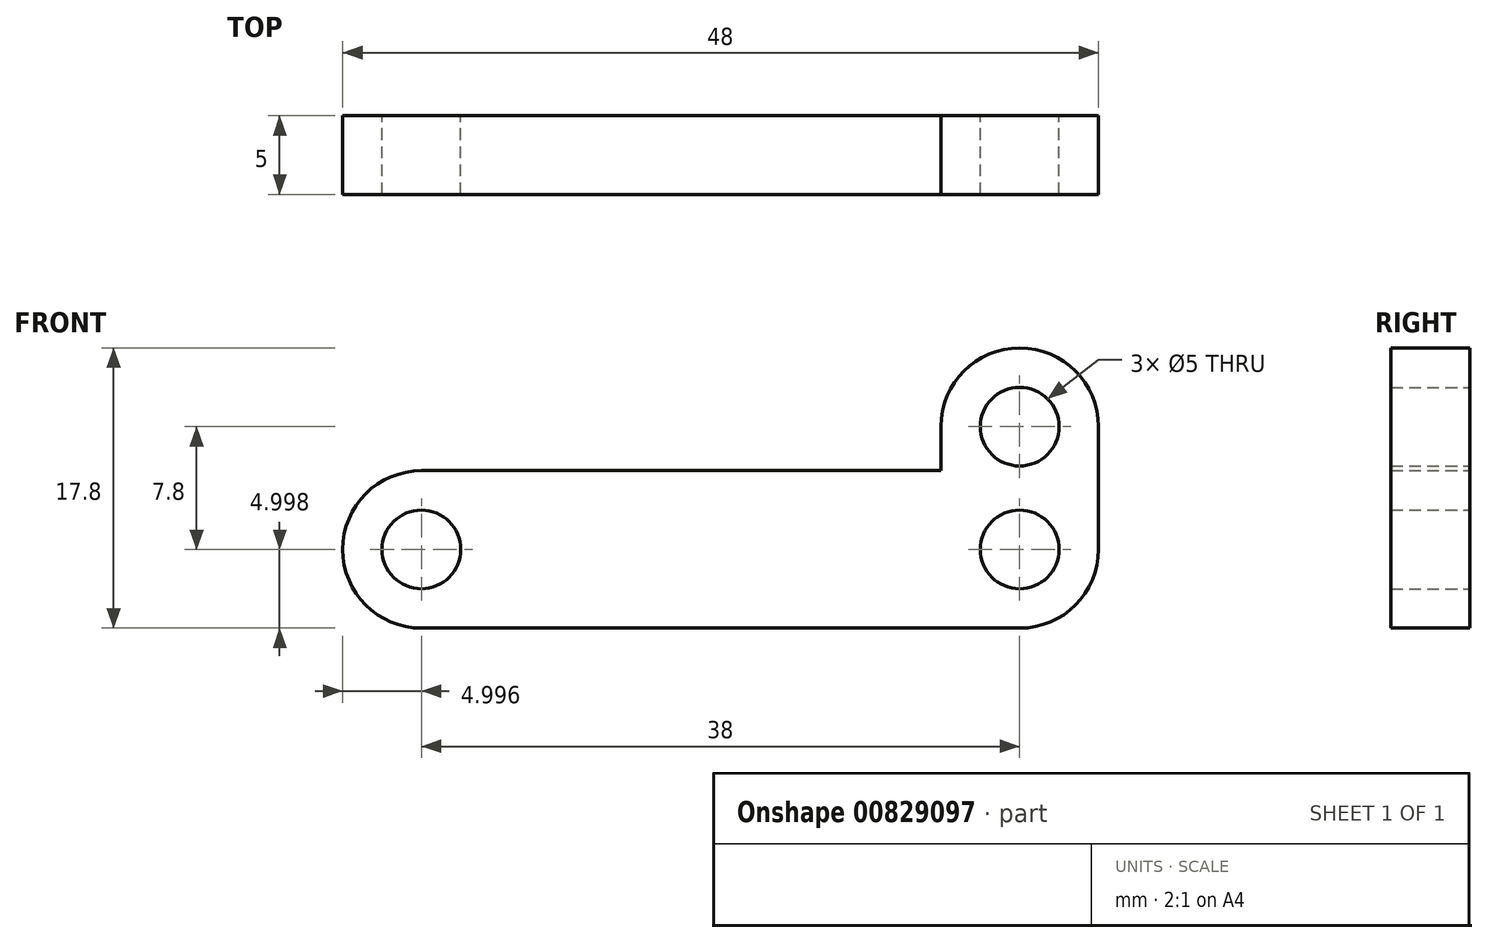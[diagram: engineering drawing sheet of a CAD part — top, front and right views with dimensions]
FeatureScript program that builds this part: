
annotation { "Feature Type Name" : "Feature", "Feature Type Description" : "" }
export const myFeature = defineFeature(function(context is Context, id is Id, definition is map)
    precondition{}
    {
        {
            var Q0;
            Q0=qCreatedBy(makeId("Front.planeOp"),FACE);
            var sketch = newSketch(context, id + "F0", { "sketchPlane" : qUnion([Q0])});
            skArc(sketch, "E0", {"start": v(-22.28, 21.13) * mm, "mid": v(-27.28, 16.13) * mm, "end": v(-22.28, 11.13) * mm});
            skArc(sketch, "E1", {"start": v(15.72, 11.13) * mm, "mid": v(19.25, 12.6) * mm, "end": v(20.72, 16.13) * mm});
            skLineSegment(sketch, "E2", {"start": v(-22.28, 21.13) * mm, "end": v(10.72, 21.13) * mm});
            skLineSegment(sketch, "E3", {"start": v(-22.28, 11.13) * mm, "end": v(15.72, 11.13) * mm});
            skCircle(sketch, "E4", {"center": v(-22.28, 16.13) * mm, "radius": 2.5 * mm});
            skArc(sketch, "E5", {"start": v(20.72, 23.93) * mm, "mid": v(15.72, 28.93) * mm, "end": v(10.72, 23.93) * mm});
            skLineSegment(sketch, "E6", {"start": v(20.72, 23.93) * mm, "end": v(20.72, 16.13) * mm});
            skLineSegment(sketch, "E7", {"start": v(10.72, 23.93) * mm, "end": v(10.72, 21.13) * mm});
            skPoint(sketch, "E8.orphan", {"position": v(15.72, 21.13) * mm});
            skCircle(sketch, "E9", {"center": v(15.72, 23.93) * mm, "radius": 2.5 * mm});
            skCircle(sketch, "E10", {"center": v(15.72, 16.13) * mm, "radius": 2.5 * mm});
            skSolve(sketch);
        }
        {
            var Q0;
            Q0 = qSketchRegion(id + "F0", true);
            extrude(context, id + "F1", {"entities" : qUnion([Q0]), "depth" : 5 * mm, "offsetDistance" : 25 * mm});
        }
    });
